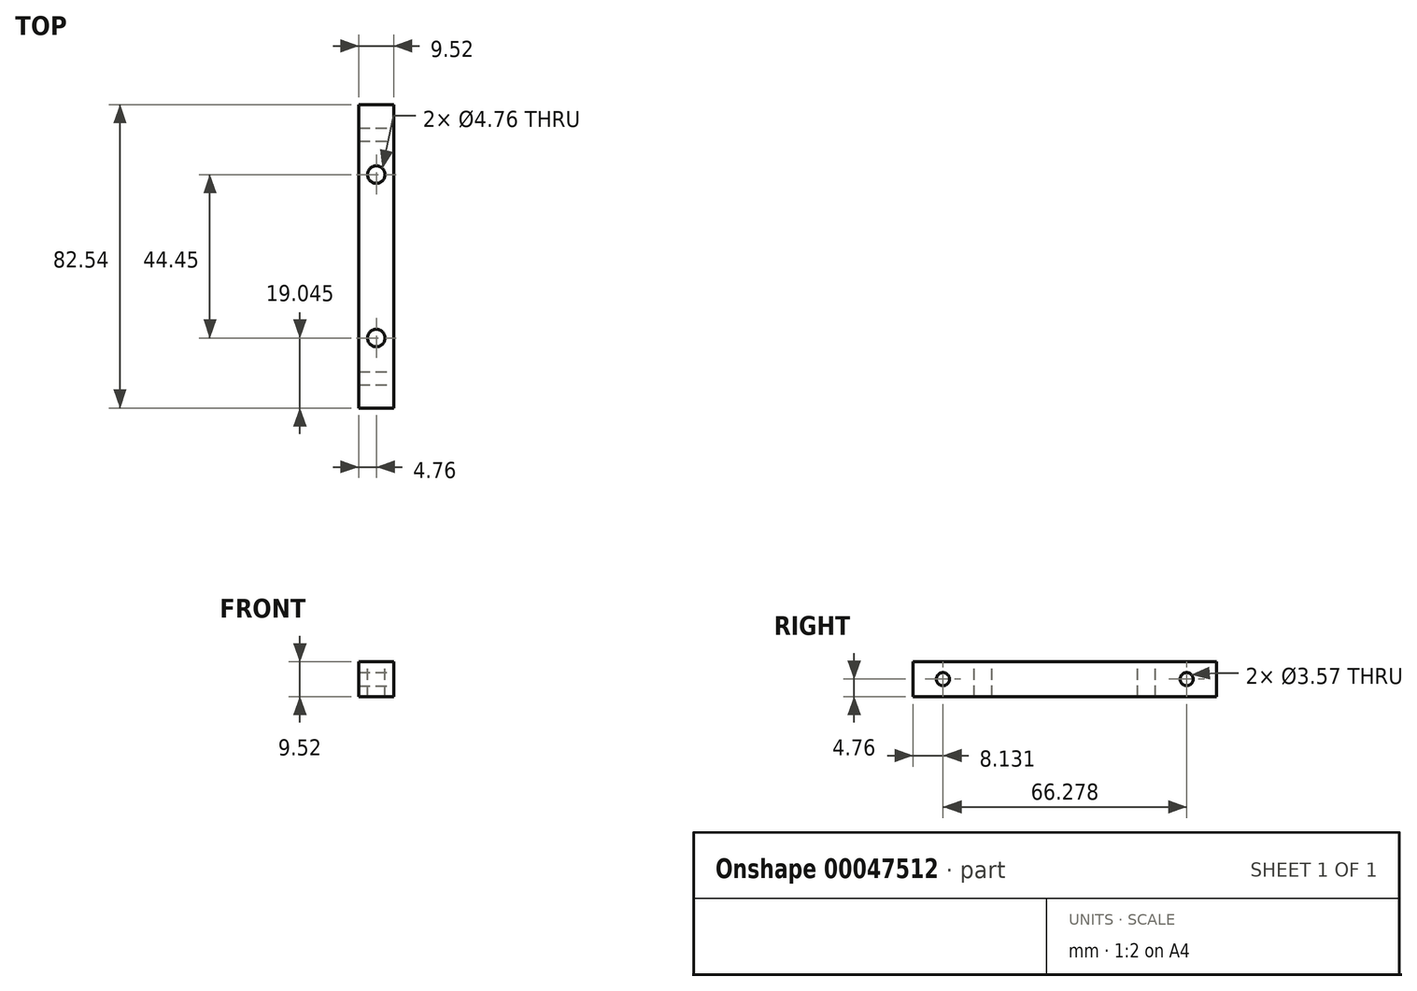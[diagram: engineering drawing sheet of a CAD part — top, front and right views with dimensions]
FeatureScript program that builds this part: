
annotation { "Feature Type Name" : "Feature", "Feature Type Description" : "" }
export const myFeature = defineFeature(function(context is Context, id is Id, definition is map)
    precondition{}
    {
        {
            var Q0;
            Q0=qCreatedBy(makeId("Front.planeOp"),FACE);
            var sketch = newSketch(context, id + "F0", { "sketchPlane" : qUnion([Q0])});
            skLineSegment(sketch, "E0.rect.bottom", {"start": v(4.76, 4.76) * mm, "end": v(-4.76, 4.76) * mm});
            skLineSegment(sketch, "E0.rect.top", {"start": v(4.76, -4.76) * mm, "end": v(-4.76, -4.76) * mm});
            skLineSegment(sketch, "E0.rect.left", {"start": v(4.76, 4.76) * mm, "end": v(4.76, -4.76) * mm});
            skLineSegment(sketch, "E0.rect.right", {"start": v(-4.76, 4.76) * mm, "end": v(-4.76, -4.76) * mm});
            skPoint(sketch, "E0.rect.middle", {"position": v(0, 0) * mm});
            skSolve(sketch);
        }
        {
            var Q0;
            Q0=makeQuery(id+"F0.imprint","IMPRINT",FACE,{"disambiguationData":[TD([[makeQuery(id+"F0.imprint","IMPRINT",EDGE,{"derivedFrom":sQuery(id+"F0.wireOp",EDGE,"E0.rect.bottom")}),1.0]])]});
            extrude(context, id + "F1", {"entities" : qUnion([Q0]), "endBound" : BoundingType.SYMMETRIC, "depth" : 82.55 * mm});
        }
        {
            var Q0;
            Q0=makeQuery(id+"F1.opExtrude","SWEPT_FACE",FACE,{"disambiguationData":[OSD([sQuery(id+"F0.wireOp",EDGE,"E0.rect.left")])]});
            var sketch = newSketch(context, id + "F2", { "sketchPlane" : qUnion([Q0])});
            skCircle(sketch, "E1", {"center": v(-33.14, 0) * mm, "radius": 1.79 * mm});
            skSolve(sketch);
        }
        {
            var Q0;
            Q0=makeQuery(id+"F2.imprint","IMPRINT",FACE,{"disambiguationData":[TD([[makeQuery(id+"F2.imprint","IMPRINT",EDGE,{"derivedFrom":sQuery(id+"F2.wireOp",EDGE,"E1")}),-1.0]])]});
            var sketch = newSketch(context, id + "F3", { "sketchPlane" : qUnion([Q0])});
            skCircle(sketch, "E2", {"center": v(33.14, 0) * mm, "radius": 1.79 * mm});
            skSolve(sketch);
        }
        {
            var Q0;
            Q0=makeQuery(id+"F2.imprint","IMPRINT",FACE,{"disambiguationData":[TD([[makeQuery(id+"F2.imprint","IMPRINT",EDGE,{"derivedFrom":sQuery(id+"F2.wireOp",EDGE,"E1")}),1.0]])]});
            extrude(context, id + "F4", {"entities" : qUnion([Q0]), "operationType" : NewBodyOperationType.REMOVE, "oppositeDirection" : true, "depth" : 9.52 * mm});
        }
        {
            var Q0;
            Q0=makeQuery(id+"F3.imprint","IMPRINT",FACE,{"disambiguationData":[TD([[makeQuery(id+"F3.imprint","IMPRINT",EDGE,{"derivedFrom":sQuery(id+"F3.wireOp",EDGE,"E2")}),1.0]])]});
            extrude(context, id + "F5", {"entities" : qUnion([Q0]), "operationType" : NewBodyOperationType.REMOVE, "oppositeDirection" : true, "depth" : 9.52 * mm});
        }
        {
            var Q0;
            Q0=makeQuery(id+"F1.opExtrude","SWEPT_FACE",FACE,{"disambiguationData":[OSD([sQuery(id+"F0.wireOp",EDGE,"E0.rect.bottom")])]});
            var sketch = newSketch(context, id + "F6", { "sketchPlane" : qUnion([Q0])});
            skCircle(sketch, "E3", {"center": v(0, 22.23) * mm, "radius": 2.38 * mm});
            skSolve(sketch);
        }
        {
            var Q0;
            Q0=makeQuery(id+"F6.imprint","IMPRINT",FACE,{"disambiguationData":[TD([[makeQuery(id+"F6.imprint","IMPRINT",EDGE,{"derivedFrom":sQuery(id+"F6.wireOp",EDGE,"E3")}),-1.0]])]});
            var sketch = newSketch(context, id + "F7", { "sketchPlane" : qUnion([Q0])});
            skCircle(sketch, "E4", {"center": v(0, -22.23) * mm, "radius": 2.38 * mm});
            skSolve(sketch);
        }
        {
            var Q0;
            Q0=makeQuery(id+"F6.imprint","IMPRINT",FACE,{"disambiguationData":[TD([[makeQuery(id+"F6.imprint","IMPRINT",EDGE,{"derivedFrom":sQuery(id+"F6.wireOp",EDGE,"E3")}),1.0]])]});
            extrude(context, id + "F8", {"entities" : qUnion([Q0]), "operationType" : NewBodyOperationType.REMOVE, "oppositeDirection" : true, "depth" : 9.52 * mm});
        }
        {
            var Q0;
            Q0=makeQuery(id+"F7.imprint","IMPRINT",FACE,{"disambiguationData":[TD([[makeQuery(id+"F7.imprint","IMPRINT",EDGE,{"derivedFrom":sQuery(id+"F7.wireOp",EDGE,"E4")}),1.0]])]});
            extrude(context, id + "F9", {"entities" : qUnion([Q0]), "operationType" : NewBodyOperationType.REMOVE, "oppositeDirection" : true, "depth" : 9.52 * mm});
        }
    });
